# Revit family: Hager-Vector-IP65-UV_Resistance-syst-DE-de
name_source: partatom
category: Electrical Equipment
units: mm (PartAtom-declared; Revit-internal decimal feet)

## family parameters
Cut with Voids When Loaded = No
Host = Face
Panel Configuration = Two Columns, Circuits Across
Part Type = Panelboard
Room Calculation Point = No
Round Connector Dimension = Use Diameter
Shared = No

## types (27) — shared parameters
EF000003 - Montageart = EV000384 - Aufputz
EF000007 - Farbe = EV000270 - grau
EF000116 - RAL-Nummer = 7035
EF000118 - Mit Montageplatte = No
EF000339 - Art der Abdeckung = EV004216 - Tür
EF001062 - EMV-Ausführung = No
EF001088 - Anbaumöglichkeit = Yes
EF001134 - DIN-Schiene = Yes
EF001596 - Werkstoff des Gehäuses = EV000139 - Kunststoff
EF004462 - Art der Schließung = EV000154 - sonstige
EF005474 - Schutzart (IP) = EV006421 - IP65
EF006244 - Transparenter Deckel/Tür = Yes
EF006306 - Mit Schloss = No
EF009212 - Ausführung Deckel = EV000116 - geschlossen
EF015776 - Erdungsklemmenblock = No
EF015777 - Neutralleiterklemmenblock = No
EF015941 - Signaldurchlassende Tür = Yes
HG000001 - Anzahl der Spalten = 1
HG000002 - Mit tür = Yes
HG000003 - Bereich = Vector
HG000005 - Dicke = 3 mm  [stored 0.00984252 ft]
HG000006 - Unterputz = No
HG000009 - Doppelflügeligen Tür = No
HG000010 - Asymmetrische Türen = No
HG000011 - Leere Reihen von unten = No
HG000017 - Distanz zwischen den Polen = 18 mm  [stored 0.0590551 ft]
Manufacturer = Hager
Type Comments = Vector
zero-valued in all types: Default Elevation, EF000218 - Einbautiefe, EF000332 - Einbauhöhe, EF000846 - Einbaubreite, HG000007 - Anzahl der leeren Spalten, HG000008 - Anzahl der leeren Reihen

## per-type parameters (varying)
| type | EF000008 - Breite | EF000040 - Höhe | EF000049 - Tiefe | EF000266 - Anzahl der Reihen | EF001131 - Innentiefe | EF002950 - Breite in Teilungseinheiten | HG000004 - Herstellerreferenz | Model |
| Aufputz IP65 B111 H175 T93 3 Teilungseinheiten - VE103PN | 111 mm | 175 mm  [stored 0.574147 ft] | 93 mm  [stored 0.305118 ft] | 1 | 93 mm  [stored 0.305118 ft] | 3 | VE103PN | VE103PN |
| Aufputz IP65 B111 H175 T93 3 Teilungseinheiten - VE103SN | 111 mm | 175 mm  [stored 0.574147 ft] | 93 mm  [stored 0.305118 ft] | 1 | 93 mm  [stored 0.305118 ft] | 3 | VE103SN | VE103SN |
| Aufputz IP65 B165 H190 T113 6 Teilungseinheiten - VE106PN | 165 mm | 190 mm | 113 mm  [stored 0.370735 ft] | 1 | 113 mm  [stored 0.370735 ft] | 6 | VE106PN | VE106PN |
| Aufputz IP65 B165 H190 T113 6 Teilungseinheiten - VE106SN | 165 mm | 190 mm | 113 mm  [stored 0.370735 ft] | 1 | 113 mm  [stored 0.370735 ft] | 6 | VE106SN | VE106SN |
| Aufputz IP65 B237 H210 T114 10 Teilungseinheiten - VE110PN | 237 mm  [stored 0.777559 ft] | 210 mm  [stored 0.688976 ft] | 114 mm  [stored 0.374016 ft] | 1 | 114 mm  [stored 0.374016 ft] | 10 | VE110PN | VE110PN |
| Aufputz IP65 B237 H210 T114 10 Teilungseinheiten - VE110SN | 237 mm  [stored 0.777559 ft] | 210 mm  [stored 0.688976 ft] | 114 mm  [stored 0.374016 ft] | 1 | 114 mm  [stored 0.374016 ft] | 10 | VE110SN | VE110SN |
| Aufputz IP65 B310 H302 T151 12 Teilungseinheiten - VE112DN | 310 mm  [stored 1.01706 ft] | 302 mm  [stored 0.990814 ft] | 151 mm  [stored 0.495407 ft] | 1 | 151 mm  [stored 0.495407 ft] | 12 | VE112DN | VE112DN |
| Aufputz IP65 B310 H302 T151 12 Teilungseinheiten - VE112PN | 310 mm  [stored 1.01706 ft] | 302 mm  [stored 0.990814 ft] | 151 mm  [stored 0.495407 ft] | 1 | 151 mm  [stored 0.495407 ft] | 12 | VE112PN | VE112PN |
| Aufputz IP65 B310 H302 T151 12 Teilungseinheiten - VE112SN | 310 mm  [stored 1.01706 ft] | 302 mm  [stored 0.990814 ft] | 151 mm  [stored 0.495407 ft] | 1 | 151 mm  [stored 0.495407 ft] | 12 | VE112SN | VE112SN |
| Aufputz IP65 B310 H427 T151 12 Teilungseinheiten - VE212DN | 310 mm  [stored 1.01706 ft] | 427 mm  [stored 1.40092 ft] | 151 mm  [stored 0.495407 ft] | 2 | 151 mm  [stored 0.495407 ft] | 12 | VE212DN | VE212DN |
| Aufputz IP65 B310 H427 T151 12 Teilungseinheiten - VE212PN | 310 mm  [stored 1.01706 ft] | 427 mm  [stored 1.40092 ft] | 151 mm  [stored 0.495407 ft] | 2 | 151 mm  [stored 0.495407 ft] | 12 | VE212PN | VE212PN |
| Aufputz IP65 B310 H427 T151 12 Teilungseinheiten - VE212SN | 310 mm  [stored 1.01706 ft] | 427 mm  [stored 1.40092 ft] | 151 mm  [stored 0.495407 ft] | 2 | 151 mm  [stored 0.495407 ft] | 12 | VE212SN | VE212SN |
| Aufputz IP65 B310 H552 T151 12 Teilungseinheiten - VE312DN | 310 mm  [stored 1.01706 ft] | 552 mm  [stored 1.81102 ft] | 151 mm  [stored 0.495407 ft] | 3 | 151 mm  [stored 0.495407 ft] | 12 | VE312DN | VE312DN |
| Aufputz IP65 B310 H552 T151 12 Teilungseinheiten - VE312PN | 310 mm  [stored 1.01706 ft] | 552 mm  [stored 1.81102 ft] | 151 mm  [stored 0.495407 ft] | 3 | 151 mm  [stored 0.495407 ft] | 12 | VE312PN | VE312PN |
| Aufputz IP65 B310 H552 T151 12 Teilungseinheiten - VE312SN | 310 mm  [stored 1.01706 ft] | 552 mm  [stored 1.81102 ft] | 151 mm  [stored 0.495407 ft] | 3 | 151 mm  [stored 0.495407 ft] | 12 | VE312SN | VE312SN |
| Aufputz IP65 B310 H677 T151 12 Teilungseinheiten - VE412DN | 310 mm  [stored 1.01706 ft] | 677 mm  [stored 2.22113 ft] | 151 mm  [stored 0.495407 ft] | 4 | 151 mm  [stored 0.495407 ft] | 12 | VE412DN | VE412DN |
| Aufputz IP65 B310 H677 T151 12 Teilungseinheiten - VE412PN | 310 mm  [stored 1.01706 ft] | 677 mm  [stored 2.22113 ft] | 151 mm  [stored 0.495407 ft] | 4 | 151 mm  [stored 0.495407 ft] | 12 | VE412PN | VE412PN |
| Aufputz IP65 B310 H677 T151 12 Teilungseinheiten - VE412SN | 310 mm  [stored 1.01706 ft] | 677 mm  [stored 2.22113 ft] | 151 mm  [stored 0.495407 ft] | 4 | 151 mm  [stored 0.495407 ft] | 12 | VE412SN | VE412SN |
| Aufputz IP65 B418 H302 T151 18 Teilungseinheiten - VE118DN | 418 mm  [stored 1.37139 ft] | 302 mm  [stored 0.990814 ft] | 151 mm  [stored 0.495407 ft] | 1 | 151 mm  [stored 0.495407 ft] | 18 | VE118DN | VE118DN |
| Aufputz IP65 B418 H302 T151 18 Teilungseinheiten - VE118PN | 418 mm  [stored 1.37139 ft] | 302 mm  [stored 0.990814 ft] | 151 mm  [stored 0.495407 ft] | 1 | 151 mm  [stored 0.495407 ft] | 18 | VE118PN | VE118PN |
| Aufputz IP65 B418 H302 T151 18 Teilungseinheiten - VE118SN | 418 mm  [stored 1.37139 ft] | 302 mm  [stored 0.990814 ft] | 151 mm  [stored 0.495407 ft] | 1 | 151 mm  [stored 0.495407 ft] | 18 | VE118SN | VE118SN |
| Aufputz IP65 B418 H452 T151 18 Teilungseinheiten - VE218DN | 418 mm  [stored 1.37139 ft] | 452 mm  [stored 1.48294 ft] | 151 mm  [stored 0.495407 ft] | 2 | 151 mm  [stored 0.495407 ft] | 18 | VE218DN | VE218DN |
| Aufputz IP65 B418 H452 T151 18 Teilungseinheiten - VE218PN | 418 mm  [stored 1.37139 ft] | 452 mm  [stored 1.48294 ft] | 151 mm  [stored 0.495407 ft] | 2 | 151 mm  [stored 0.495407 ft] | 18 | VE218PN | VE218PN |
| Aufputz IP65 B418 H452 T151 18 Teilungseinheiten - VE218SN | 418 mm  [stored 1.37139 ft] | 452 mm  [stored 1.48294 ft] | 151 mm  [stored 0.495407 ft] | 2 | 151 mm  [stored 0.495407 ft] | 18 | VE218SN | VE218SN |
| Aufputz IP65 B418 H602 T151 18 Teilungseinheiten - VE318DN | 418 mm  [stored 1.37139 ft] | 602 mm  [stored 1.97507 ft] | 151 mm  [stored 0.495407 ft] | 3 | 151 mm  [stored 0.495407 ft] | 18 | VE318DN | VE318DN |
| Aufputz IP65 B418 H602 T151 18 Teilungseinheiten - VE318PN | 418 mm  [stored 1.37139 ft] | 602 mm  [stored 1.97507 ft] | 151 mm  [stored 0.495407 ft] | 3 | 151 mm  [stored 0.495407 ft] | 18 | VE318PN | VE318PN |
| Aufputz IP65 B418 H602 T151 18 Teilungseinheiten - VE318SN | 418 mm  [stored 1.37139 ft] | 602 mm  [stored 1.97507 ft] | 151 mm  [stored 0.495407 ft] | 3 | 151 mm  [stored 0.495407 ft] | 18 | VE318SN | VE318SN |

note: [stored X ft] marks values corroborated as IEEE doubles in the binary element streams (Revit-internal decimal feet)

## geometry (parser evidence)
native form markers: Sweep x17
no freeform markers — native parametric forms only
